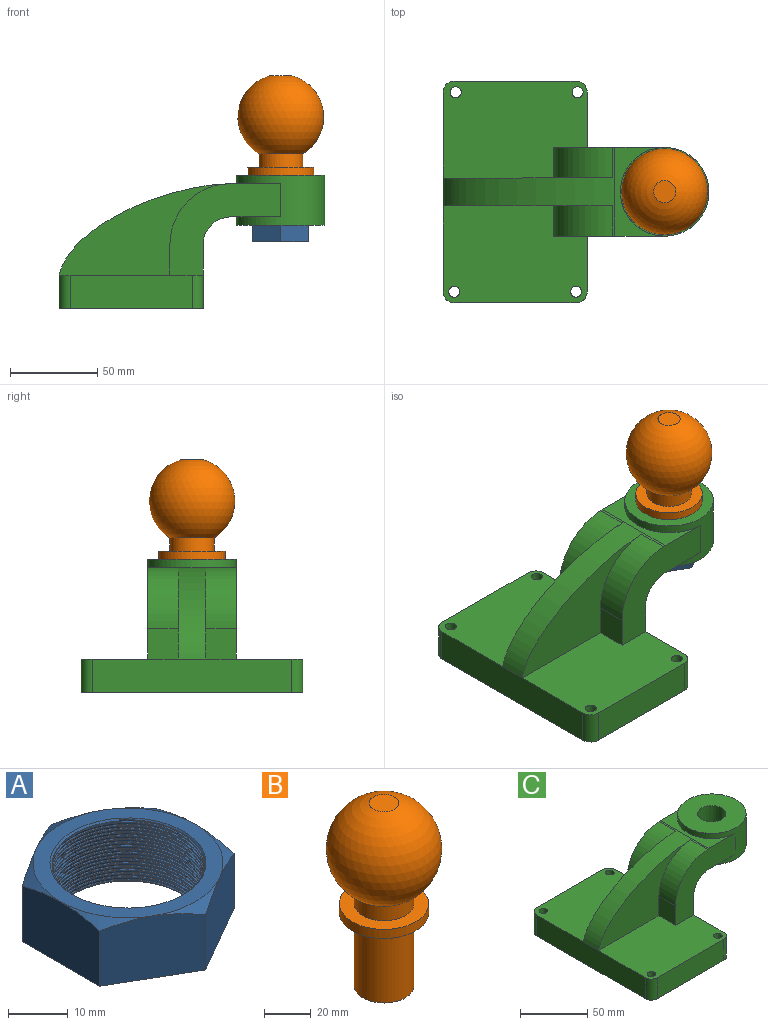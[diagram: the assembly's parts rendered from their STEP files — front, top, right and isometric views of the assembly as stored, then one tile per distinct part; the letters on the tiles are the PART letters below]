
ASSEMBLY  parts=3 mates=2
PART A: 19 faces, bbox 38.2x38.2x14.8 mm
  f0: cylinder r=12.7mm len=25.4mm, axis (0,0,-1), area -6.4mm2, adj f1,f9,f16,f17,f18
  f1: cone r=12.7mm half-angle=45deg, axis (0,0,1), area 35.3mm2, adj f0,f2,f17,f18
  f2: plane 31.75x31.75mm, normal (0,0,1), area 257.7mm2, adj f1,f10,f11,f12,f13,f14,f15
  f3: plane 17.38x14.21mm, normal (0.5,0.87,0), area 223.9mm2, adj f4,f8,f9,f10,f15
  f4: plane 17.38x14.21mm, normal (-0.5,0.87,0), area 223.9mm2, adj f3,f5,f9,f14,f15
  f5: plane 19.86x14.22mm, normal (-1,0,0), area 223.9mm2, adj f4,f6,f9,f13,f14
  f6: plane 17.38x14.21mm, normal (-0.5,-0.87,0), area 223.9mm2, adj f5,f7,f9,f12,f13
  f7: plane 17.38x14.21mm, normal (0.5,-0.87,0), area 223.9mm2, adj f6,f8,f9,f11,f12
  f8: plane 19.86x14.22mm, normal (1,0,0), area 223.9mm2, adj f3,f7,f9,f10,f11
  f9: plane 36.66x31.75mm, normal (0,0,-1), area 354.6mm2, adj f0,f3,f4,f5,f6,f7,f8,f16
  f10: cone r=18.35mm half-angle=60deg, axis (0,0,-1), area 24.8mm2, adj f2,f3,f8
  f11: cone r=18.35mm half-angle=60deg, axis (0,0,-1), area 24.8mm2, adj f2,f7,f8
  f12: cone r=18.35mm half-angle=60deg, axis (0,0,-1), area 24.8mm2, adj f2,f6,f7
  f13: cone r=18.35mm half-angle=60deg, axis (0,0,-1), area 24.8mm2, adj f2,f5,f6
  f14: cone r=18.35mm half-angle=60deg, axis (0,0,-1), area 24.8mm2, adj f2,f4,f5
  f15: cone r=18.35mm half-angle=60deg, axis (0,0,-1), area 24.8mm2, adj f2,f3,f4
  f16: bspline ~30.12x26.09mm, area 477.3mm2, adj f0,f9,f17,f18
  f17: bspline ~30.12x26.09mm, area 974.9mm2, adj f0,f1,f9,f16,f18
  f18: plane 0.38x0.27mm, normal (0.78,-0.62,0), area 0.1mm2, adj f0,f1,f16,f17
PART B: 8 faces, bbox 49.2x49.2x95.3 mm
  f0: plane 12.7x12.7mm, normal (0,0,1), area 126.7mm2, adj f7
  f1: plane 25.4x25.4mm, normal (0,0,-1), area 506.7mm2, adj f2
  f2: cylinder r=12.7mm len=38.1mm, axis (0,0,1), area 3040.2mm2, adj f1,f3
  f3: plane 38.1x38.1mm, normal (0,0,-1), area 633.4mm2, adj f2,f4
  f4: cylinder r=19.05mm len=38.1mm, axis (0,0,1), area 570mm2, adj f3,f5
  f5: plane 38.1x38.1mm, normal (0,0,1), area 633.4mm2, adj f4,f6
  f6: cylinder r=12.7mm len=25.4mm, axis (0,0,1), area 601.6mm2, adj f5,f7
  f7: sphere r=24.61mm, area 6933.8mm2, adj f0,f6
PART C: 31 faces, bbox 152.4x127x76.2 mm
  f0: plane 17.48x17.46mm, normal (-1,0,0), area 305.2mm2, adj f1,f2,f16,f18
  f1: plane 82.55x55.56mm, normal (0,0,1), area 4173.4mm2, adj f0,f4,f5,f8,f16,f18,f22,f23
  f2: cylinder r=34.92mm len=34.89mm, axis (0,1,0), area 932.2mm2, adj f0,f10,f16,f18
  f3: plane 82.55x55.56mm, normal (0,0,1), area 4173.4mm2, adj f4,f5,f7,f12,f15,f17,f24,f25
  f4: plane 114.3x36.53mm, normal (1,0,0), area 3065.2mm2, adj f1,f3,f6,f13,f15,f16,f23,f25
  f5: plane 114.3x19.05mm, normal (-1,0,0), area 2177.4mm2, adj f1,f3,f6,f10,f22,f24
  f6: plane 127x82.55mm, normal (0,0,-1), area 10322.6mm2, adj f4,f5,f7,f8,f22,f23,f24,f25
  f7: plane 69.85x19.05mm, normal (0,-1,0), area 1330.6mm2, adj f3,f6,f24,f25
  f8: plane 69.85x19.05mm, normal (0,1,0), area 1330.6mm2, adj f1,f6,f22,f23
  f9: plane 50.8x28.58mm, normal (0,0,1), area 438.2mm2, adj f10,f15,f16,f20
  f10: extruded ~98.43x52.4mm, area 1914.5mm2, adj f2,f5,f9,f11,f15,f16,f17,f18
  f11: cylinder r=34.92mm len=34.89mm, axis (0,1,0), area 932.2mm2, adj f10,f12,f15,f17
  f12: plane 17.48x17.46mm, normal (-1,0,0), area 305.2mm2, adj f3,f11,f15,f17
  f13: cylinder r=15.88mm len=50.8mm, axis (0,1,0), area 1266.8mm2, adj f4,f14,f15,f16
  f14: plane 50.8x28.58mm, normal (0,0,-1), area 438.2mm2, adj f13,f15,f16,f20
  f15: plane 63.5x52.4mm, normal (0,-1,0), area 1637.3mm2, adj f3,f4,f9,f10,f11,f12,f13,f14
  f16: plane 63.5x52.4mm, normal (0,1,0), area 1637.3mm2, adj f0,f1,f2,f4,f9,f10,f13,f14
  f17: plane 98.43x52.4mm, normal (0,-1,0), area 2158mm2, adj f3,f10,f11,f12
  f18: plane 98.43x52.4mm, normal (0,1,0), area 2158mm2, adj f0,f1,f2,f10
  f19: plane 50.8x50.8mm, normal (0,0,-1), area 1580.1mm2, adj f20,f26
  f20: cylinder r=25.4mm len=50.8mm, axis (0,0,-1), area 3040.2mm2, adj f9,f14,f15,f16,f19,f21
  f21: plane 50.8x50.8mm, normal (0,0,1), area 1685.2mm2, adj f20,f26
  f22: cylinder r=6.35mm len=19.05mm, axis (0,0,-1), area 190mm2, adj f1,f5,f6,f8
  f23: cylinder r=6.35mm len=19.05mm, axis (0,0,1), area 190mm2, adj f1,f4,f6,f8
  f24: cylinder r=6.35mm len=19.05mm, axis (0,0,1), area 190mm2, adj f3,f5,f6,f7
  f25: cylinder r=6.35mm len=19.05mm, axis (0,0,-1), area 190mm2, adj f3,f4,f6,f7
  f26: cone r=10.43mm half-angle=3deg, axis (0,0,-1), area 2009.4mm2, adj f19,f21
  f27: cylinder r=3.17mm len=19.05mm, axis (0,0,1), area 380mm2, adj f3,f6
  f28: cylinder r=3.17mm len=19.05mm, axis (0,0,1), area 380mm2, adj f3,f6
  f29: cylinder r=3.17mm len=19.05mm, axis (0,0,1), area 380mm2, adj f1,f6
  f30: cylinder r=3.17mm len=19.05mm, axis (0,0,1), area 380mm2, adj f1,f6
PLACE A t=(164.76,0,66.96)mm
PLACE B at identity
PLACE C t=(79.03,0,37.34)mm
MATE fastened C.f20 <-> B.f2  axis (0,0,-1) through (164.76,0,105.06)mm
MATE fastened A.f0 <-> B.f2  axis (0,0,1) through (164.76,0,79.66)mm
